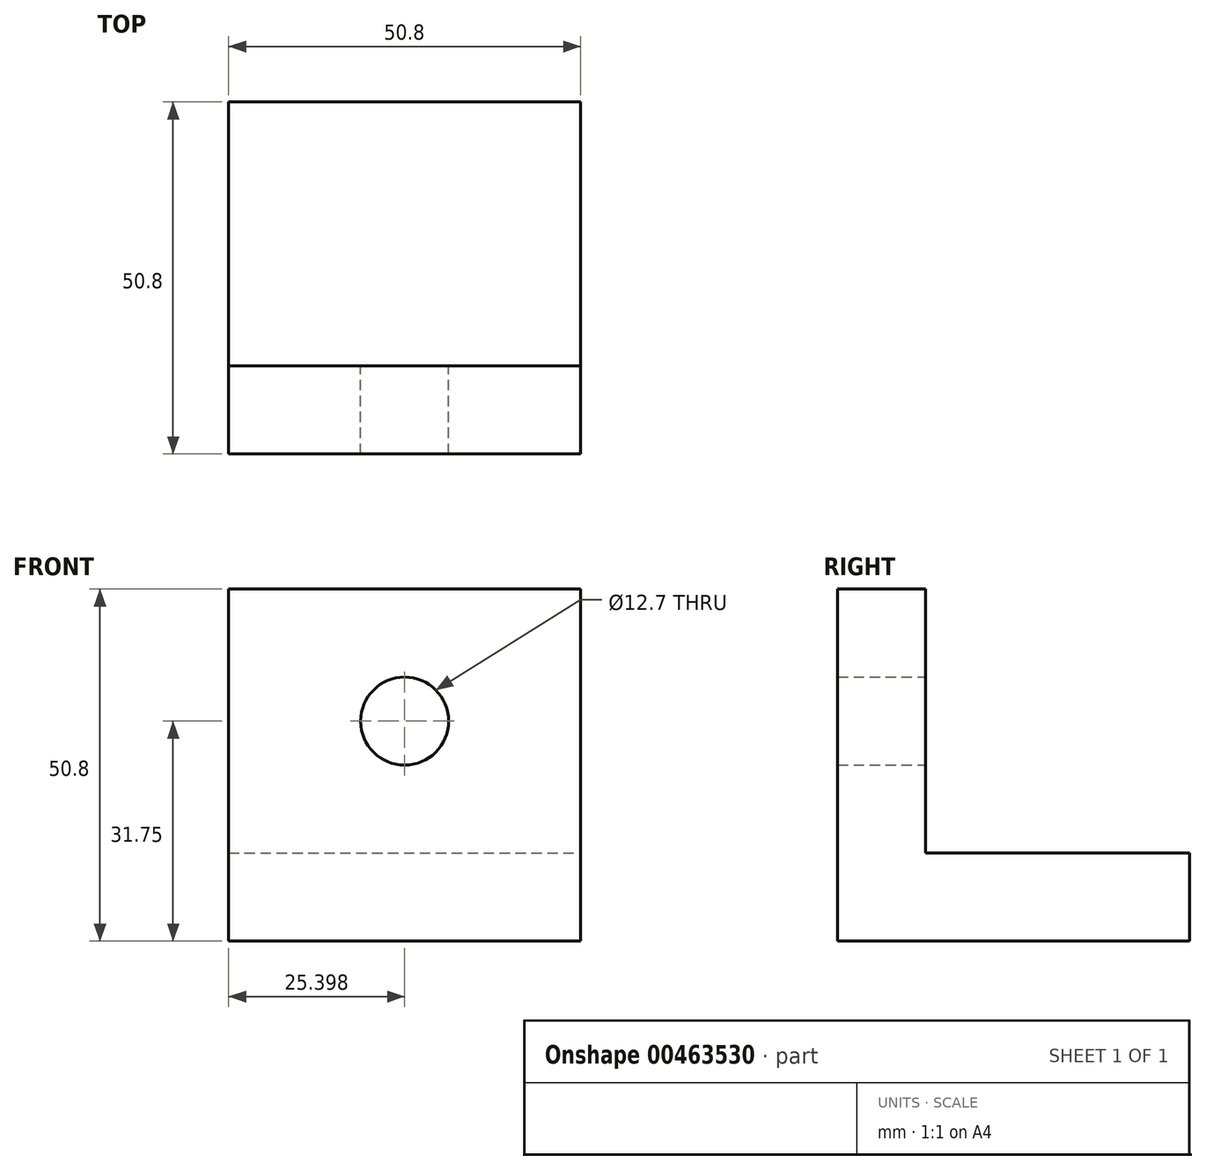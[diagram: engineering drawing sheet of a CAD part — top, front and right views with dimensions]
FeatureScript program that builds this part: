
annotation { "Feature Type Name" : "Feature", "Feature Type Description" : "" }
export const myFeature = defineFeature(function(context is Context, id is Id, definition is map)
    precondition{}
    {
        {
            var Q0;
            Q0=qCreatedBy(makeId("Top.planeOp"),FACE);
            var sketch = newSketch(context, id + "F0", { "sketchPlane" : qUnion([Q0])});
            skLineSegment(sketch, "E0.bottom", {"start": v(-39.92, 20.7) * mm, "end": v(10.88, 20.7) * mm});
            skLineSegment(sketch, "E0.top", {"start": v(-39.92, -30.1) * mm, "end": v(10.88, -30.1) * mm});
            skLineSegment(sketch, "E0.left", {"start": v(-39.92, 20.7) * mm, "end": v(-39.92, -30.1) * mm});
            skLineSegment(sketch, "E0.right", {"start": v(10.88, 20.7) * mm, "end": v(10.88, -30.1) * mm});
            skLineSegment(sketch, "E1", {"start": v(-14.52, -30.1) * mm, "end": v(-14.52, -17.4) * mm, "construction": true});
            skLineSegment(sketch, "E2", {"start": v(-39.92, -17.4) * mm, "end": v(10.88, -17.4) * mm});
            skSolve(sketch);
        }
        {
            var Q0;
            {var subQ0=sQuery(id+"F0.wireOp",EDGE,"E0.bottom");Q0=makeQuery(id+"F0.imprint","IMPRINT",FACE,{"disambiguationData":[TD([[makeQuery(id+"F0.imprint","IMPRINT",EDGE,{"derivedFrom":subQ0}),-1.0]])]});}
            extrude(context, id + "F1", {"entities" : qUnion([Q0]), "depth" : 12.7 * mm});
        }
        {
            var Q0;
            {var subQ0=sQuery(id+"F0.wireOp",EDGE,"E0.top");Q0=makeQuery(id+"F0.imprint","IMPRINT",FACE,{"disambiguationData":[TD([[makeQuery(id+"F0.imprint","IMPRINT",EDGE,{"derivedFrom":subQ0}),1.0]])]});}
            extrude(context, id + "F2", {"entities" : qUnion([Q0]), "operationType" : NewBodyOperationType.ADD, "depth" : 50.8 * mm});
        }
        {
            var Q0;
            Q0=makeQuery(id+"F2.opExtrude","SWEPT_FACE",FACE,{"disambiguationData":[OSD([sQuery(id+"F0.wireOp",EDGE,"E2")])]});
            var sketch = newSketch(context, id + "F3", { "sketchPlane" : qUnion([Q0])});
            skCircle(sketch, "E3", {"center": v(14.52, 31.75) * mm, "radius": 6.35 * mm});
            skPoint(sketch, "E3.centerSnap0", {"position": v(39.92, 31.75) * mm});
            skPoint(sketch, "E3.centerSnap1", {"position": v(14.52, 50.8) * mm});
            skSolve(sketch);
        }
        {
            var Q0;
            Q0 = qSketchRegion(id + "F3", true);
            extrude(context, id + "F4", {"entities" : qUnion([Q0]), "operationType" : NewBodyOperationType.REMOVE, "oppositeDirection" : true, "depth" : 25.4 * mm});
        }
    });
